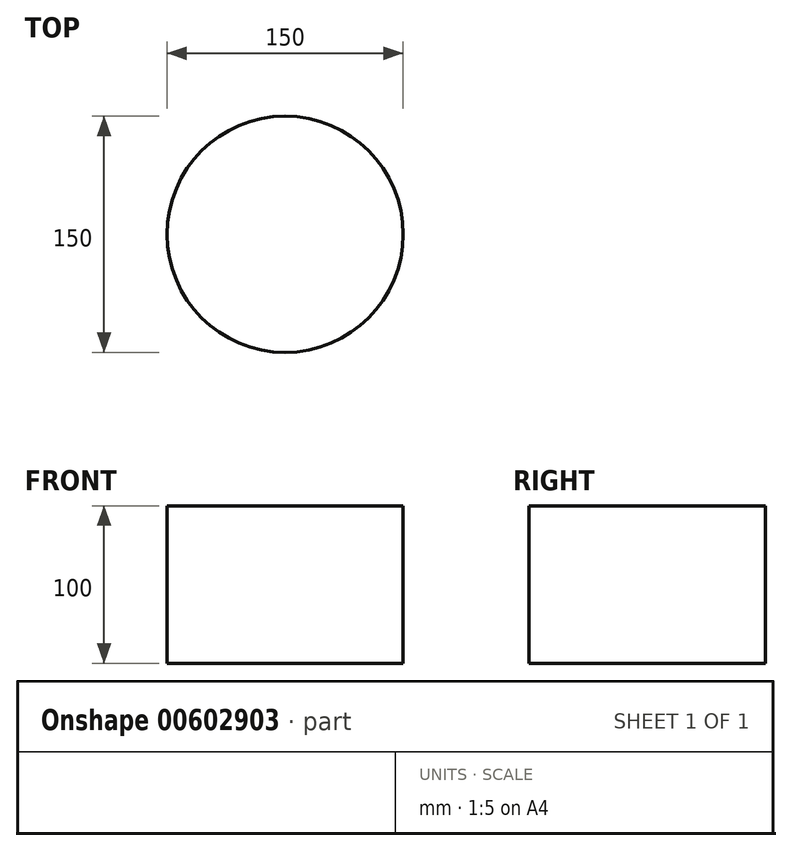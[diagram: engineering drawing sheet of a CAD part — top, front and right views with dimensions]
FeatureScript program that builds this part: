
annotation { "Feature Type Name" : "Feature", "Feature Type Description" : "" }
export const myFeature = defineFeature(function(context is Context, id is Id, definition is map)
    precondition{}
    {
        {
            var Q0;
            Q0=qCreatedBy(makeId("Top.planeOp"),FACE);
            var sketch = newSketch(context, id + "F0", { "sketchPlane" : qUnion([Q0])});
            skCircle(sketch, "E0", {"center": v(0, 0) * mm, "radius": 75 * mm});
            skSolve(sketch);
        }
        {
            var Q0;
            Q0 = qSketchRegion(id + "F0", true);
            extrude(context, id + "F1", {"entities" : qUnion([Q0]), "depth" : 100 * mm, "offsetDistance" : 25 * mm});
        }
    });
